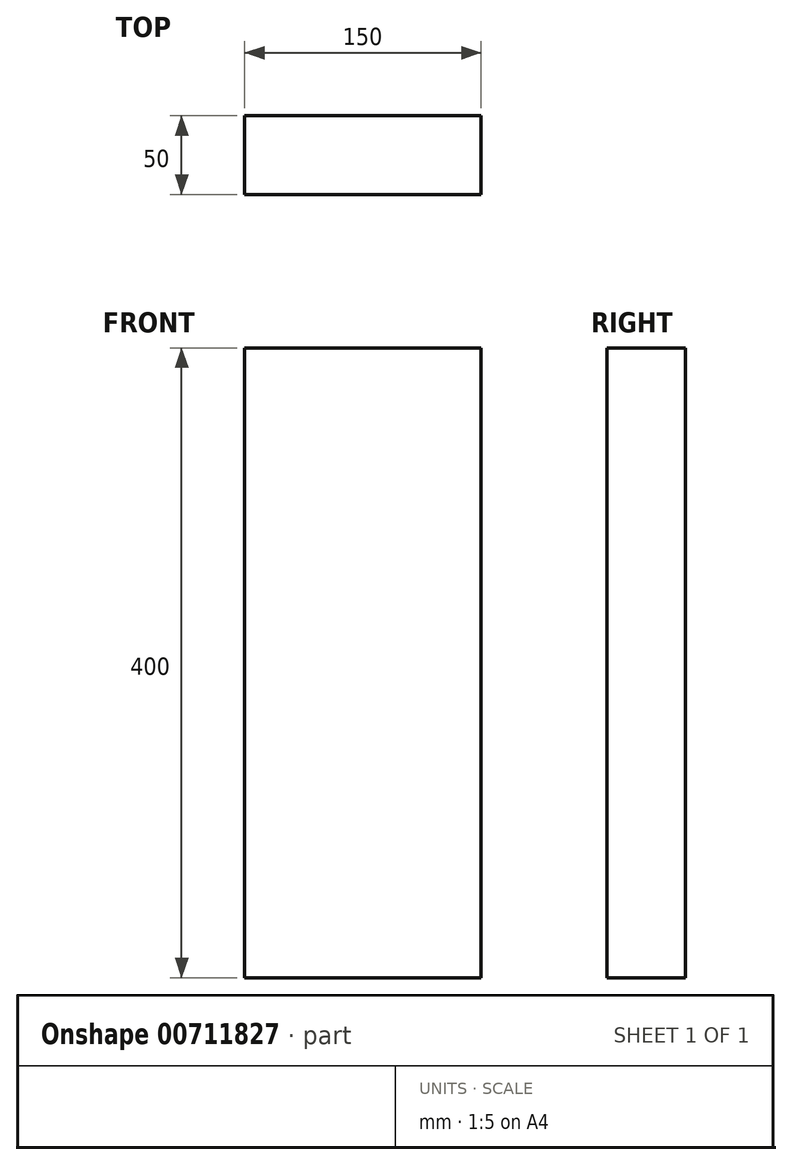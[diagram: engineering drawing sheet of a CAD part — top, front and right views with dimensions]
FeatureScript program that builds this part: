
annotation { "Feature Type Name" : "Feature", "Feature Type Description" : "" }
export const myFeature = defineFeature(function(context is Context, id is Id, definition is map)
    precondition{}
    {
        {
            var Q0;
            Q0=qCreatedBy(makeId("Front.planeOp"),FACE);
            var sketch = newSketch(context, id + "F0", { "sketchPlane" : qUnion([Q0])});
            skLineSegment(sketch, "E0.bottom", {"start": v(0, 0) * mm, "end": v(150, 0) * mm});
            skLineSegment(sketch, "E0.top", {"start": v(0, 400) * mm, "end": v(150, 400) * mm});
            skLineSegment(sketch, "E0.left", {"start": v(0, 0) * mm, "end": v(0, 400) * mm});
            skLineSegment(sketch, "E0.right", {"start": v(150, 0) * mm, "end": v(150, 400) * mm});
            skSolve(sketch);
        }
        {
            var Q0;
            Q0 = qSketchRegion(id + "F0", true);
            extrude(context, id + "F1", {"entities" : qUnion([Q0]), "depth" : 50 * mm, "offsetDistance" : 25 * mm});
        }
    });
